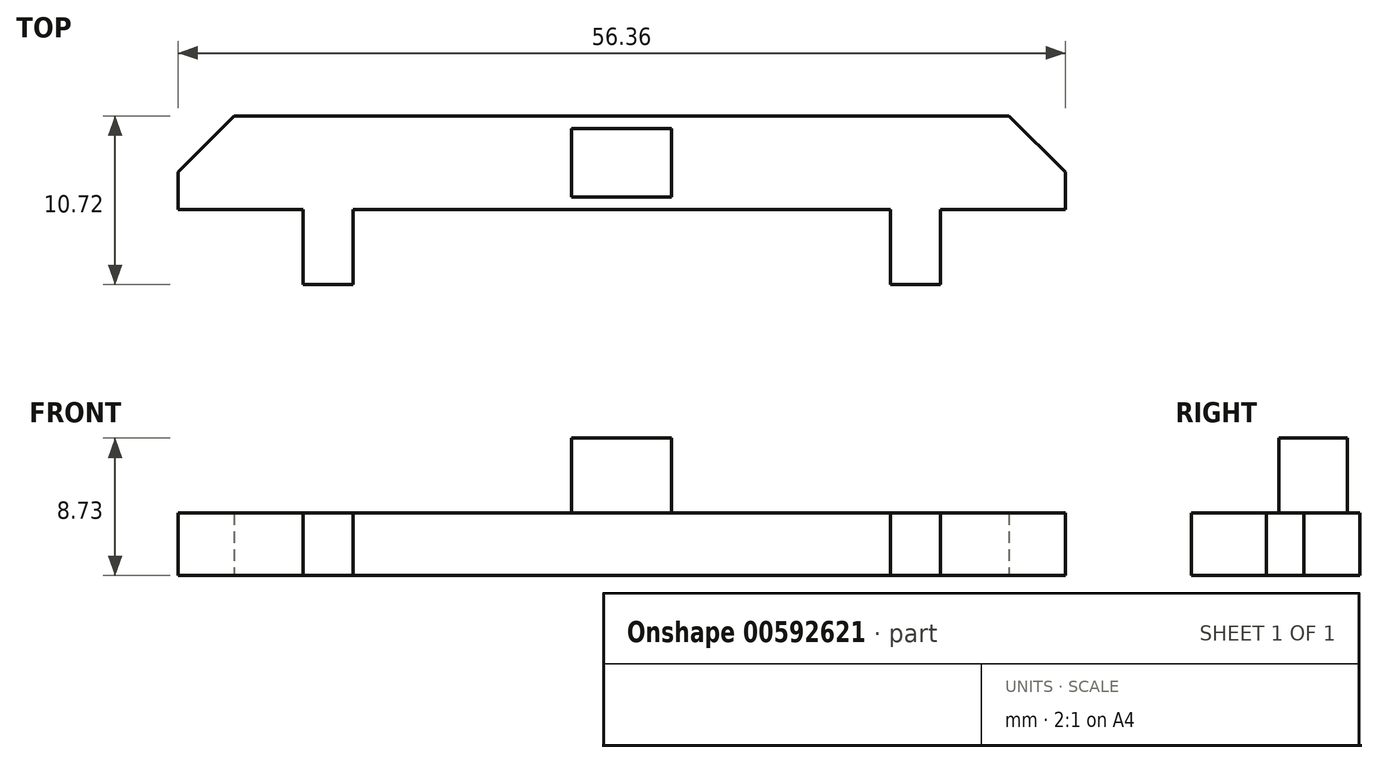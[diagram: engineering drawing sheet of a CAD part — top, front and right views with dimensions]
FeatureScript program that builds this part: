
annotation { "Feature Type Name" : "Feature", "Feature Type Description" : "" }
export const myFeature = defineFeature(function(context is Context, id is Id, definition is map)
    precondition{}
    {
        {
            var Q0;
            Q0=qCreatedBy(makeId("Top.planeOp"),FACE);
            var sketch = newSketch(context, id + "F0", { "sketchPlane" : qUnion([Q0])});
            skLineSegment(sketch, "E0.bottom", {"start": v(0, 2.98) * mm, "end": v(-24.6, 2.98) * mm});
            skLineSegment(sketch, "E0.top", {"start": v(0, -2.98) * mm, "end": v(-17.07, -2.98) * mm});
            skLineSegment(sketch, "E0.right", {"start": v(-28.18, -0.6) * mm, "end": v(-28.18, -2.98) * mm});
            skPoint(sketch, "E0.middle", {"position": v(0, 0) * mm});
            skLineSegment(sketch, "E1.top", {"start": v(-20.24, -7.74) * mm, "end": v(-17.07, -7.74) * mm});
            skLineSegment(sketch, "E1.left", {"start": v(-20.24, -2.98) * mm, "end": v(-20.24, -7.74) * mm});
            skLineSegment(sketch, "E1.right", {"start": v(-17.07, -2.98) * mm, "end": v(-17.07, -7.74) * mm});
            skPoint(sketch, "E0.left.start.orphan", {"position": v(28.18, 2.98) * mm});
            skPoint(sketch, "E2.orphan", {"position": v(28.18, -2.98) * mm});
            skLineSegment(sketch, "E3.trimOffspring", {"start": v(-20.24, -2.98) * mm, "end": v(-28.18, -2.98) * mm});
            skLineSegment(sketch, "E4", {"start": v(-28.18, -0.6) * mm, "end": v(-24.6, 2.98) * mm});
            skPoint(sketch, "E5.orphan", {"position": v(-28.18, 2.98) * mm});
            skLineSegment(sketch, "E6.MirrorCS", {"start": v(0, 2.98) * mm, "end": v(24.6, 2.98) * mm});
            skLineSegment(sketch, "E7.MirrorCS", {"start": v(20.24, -2.98) * mm, "end": v(28.18, -2.98) * mm});
            skLineSegment(sketch, "E8.MirrorCS", {"start": v(17.07, -2.98) * mm, "end": v(17.07, -7.74) * mm});
            skLineSegment(sketch, "E9.MirrorCS", {"start": v(20.24, -2.98) * mm, "end": v(20.24, -7.74) * mm});
            skLineSegment(sketch, "E10.MirrorCS", {"start": v(28.18, -0.6) * mm, "end": v(28.18, -2.98) * mm});
            skLineSegment(sketch, "E11.MirrorCS", {"start": v(28.18, -0.6) * mm, "end": v(24.6, 2.98) * mm});
            skLineSegment(sketch, "E12.MirrorCS", {"start": v(20.24, -7.74) * mm, "end": v(17.07, -7.74) * mm});
            skLineSegment(sketch, "E13.MirrorCS", {"start": v(0, -2.98) * mm, "end": v(17.07, -2.98) * mm});
            skSolve(sketch);
        }
        {
            var Q0;
            Q0=makeQuery(id+"F0.imprint","IMPRINT",FACE,{"disambiguationData":[TD([[makeQuery(id+"F0.imprint","IMPRINT",EDGE,{"derivedFrom":sQuery(id+"F0.wireOp",EDGE,"E0.bottom")}),1.0]])]});
            extrude(context, id + "F1", {"entities" : qUnion([Q0]), "depth" : 3.97 * mm, "offsetDistance" : 25.4 * mm});
        }
        {
            var Q0;
            Q0=makeQuery(id+"F1.opExtrude","CAP_FACE",FACE,{"disambiguationData":[OSD([sQuery(id+"F0.wireOp",EDGE,"E0.bottom"),sQuery(id+"F0.wireOp",EDGE,"E0.top"),sQuery(id+"F0.wireOp",EDGE,"E0.right"),sQuery(id+"F0.wireOp",EDGE,"E1.top"),sQuery(id+"F0.wireOp",EDGE,"E1.left"),sQuery(id+"F0.wireOp",EDGE,"E1.right"),sQuery(id+"F0.wireOp",EDGE,"E3.trimOffspring"),sQuery(id+"F0.wireOp",EDGE,"E4"),sQuery(id+"F0.wireOp",EDGE,"E6.MirrorCS"),sQuery(id+"F0.wireOp",EDGE,"E7.MirrorCS"),sQuery(id+"F0.wireOp",EDGE,"E8.MirrorCS"),sQuery(id+"F0.wireOp",EDGE,"E9.MirrorCS"),sQuery(id+"F0.wireOp",EDGE,"E10.MirrorCS"),sQuery(id+"F0.wireOp",EDGE,"E11.MirrorCS"),sQuery(id+"F0.wireOp",EDGE,"E12.MirrorCS"),sQuery(id+"F0.wireOp",EDGE,"E13.MirrorCS")])],"isStart":false});
            var sketch = newSketch(context, id + "F2", { "sketchPlane" : qUnion([Q0])});
            skLineSegment(sketch, "E14.bottom", {"start": v(3.18, 2.18) * mm, "end": v(-3.18, 2.18) * mm});
            skLineSegment(sketch, "E14.top", {"start": v(3.18, -2.18) * mm, "end": v(-3.18, -2.18) * mm});
            skLineSegment(sketch, "E14.left", {"start": v(3.18, 2.18) * mm, "end": v(3.18, -2.18) * mm});
            skLineSegment(sketch, "E14.right", {"start": v(-3.18, 2.18) * mm, "end": v(-3.18, -2.18) * mm});
            skPoint(sketch, "E14.middle", {"position": v(0, 0) * mm});
            skSolve(sketch);
        }
        {
            var Q0;
            Q0=makeQuery(id+"F2.imprint","IMPRINT",FACE,{"disambiguationData":[TD([[makeQuery(id+"F2.imprint","IMPRINT",EDGE,{"derivedFrom":sQuery(id+"F2.wireOp",EDGE,"E14.bottom")}),1.0]])]});
            extrude(context, id + "F3", {"entities" : qUnion([Q0]), "operationType" : NewBodyOperationType.ADD, "depth" : 4.76 * mm, "offsetDistance" : 25.4 * mm});
        }
    });
